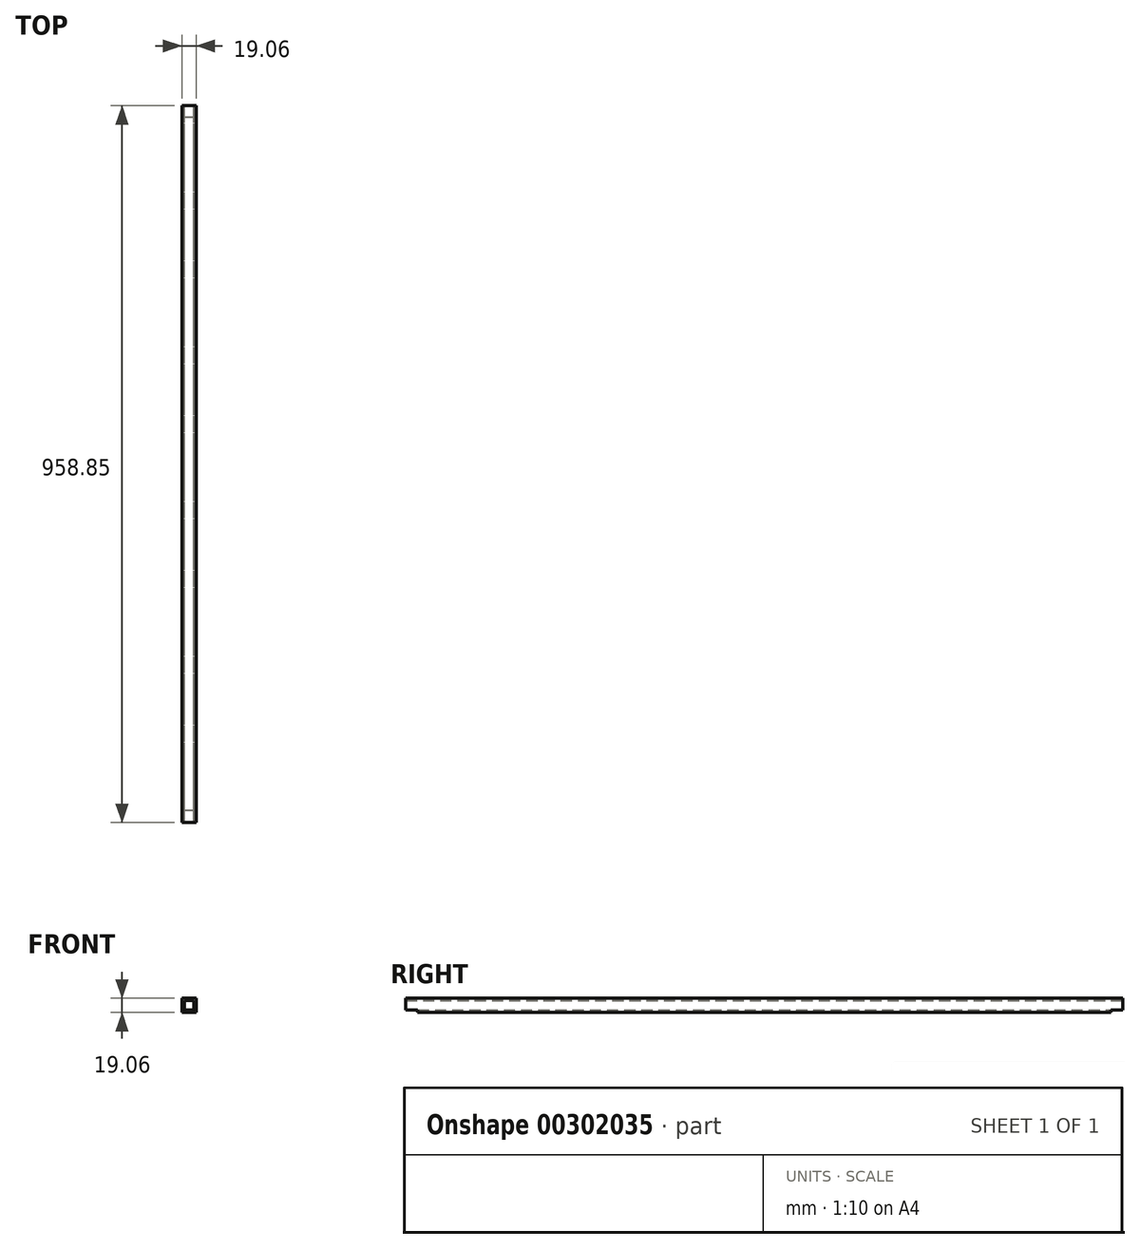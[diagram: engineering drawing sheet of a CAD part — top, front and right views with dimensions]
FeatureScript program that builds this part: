
annotation { "Feature Type Name" : "Feature", "Feature Type Description" : "" }
export const myFeature = defineFeature(function(context is Context, id is Id, definition is map)
    precondition{}
    {
        {
            var Q0;
            Q0=qCreatedBy(makeId("Front.planeOp"),FACE);
            var sketch = newSketch(context, id + "F0", { "sketchPlane" : qUnion([Q0])});
            skLineSegment(sketch, "E0.bottom", {"start": v(9.52, 9.53) * mm, "end": v(-9.53, 9.52) * mm});
            skLineSegment(sketch, "E0.top", {"start": v(9.53, -9.52) * mm, "end": v(-9.52, -9.53) * mm});
            skLineSegment(sketch, "E0.left", {"start": v(9.52, 9.53) * mm, "end": v(9.53, -9.52) * mm});
            skLineSegment(sketch, "E0.right", {"start": v(-9.53, 9.52) * mm, "end": v(-9.52, -9.53) * mm});
            skPoint(sketch, "E0.middle", {"position": v(0, 0) * mm});
            skLineSegment(sketch, "E1.bottom", {"start": v(6.35, 6.35) * mm, "end": v(-6.35, 6.35) * mm});
            skLineSegment(sketch, "E1.top", {"start": v(6.35, -6.35) * mm, "end": v(-6.35, -6.35) * mm});
            skLineSegment(sketch, "E1.left", {"start": v(6.35, 6.35) * mm, "end": v(6.35, -6.35) * mm});
            skLineSegment(sketch, "E1.right", {"start": v(-6.35, 6.35) * mm, "end": v(-6.35, -6.35) * mm});
            skSolve(sketch);
        }
        {
            var Q0;
            Q0=qSketchRegion(id+"F0",true);
            extrude(context, id + "F1", {"entities" : qUnion([Q0]), "depth" : 958.85 * mm});
        }
        {
            var Q0;
            Q0=makeQuery(id+"F1.opExtrude","SWEPT_FACE",FACE,{"disambiguationData":[OSD([sQuery(id+"F0.wireOp",EDGE,"E0.right")])]});
            var sketch = newSketch(context, id + "F2", { "sketchPlane" : qUnion([Q0])});
            skLineSegment(sketch, "E2.bottom", {"start": v(0, -9.53) * mm, "end": v(15.88, -9.53) * mm});
            skLineSegment(sketch, "E2.top", {"start": v(0, -6.35) * mm, "end": v(15.88, -6.35) * mm});
            skLineSegment(sketch, "E2.left", {"start": v(0, -9.53) * mm, "end": v(0, -6.35) * mm});
            skLineSegment(sketch, "E2.right", {"start": v(15.88, -9.53) * mm, "end": v(15.88, -6.35) * mm});
            skLineSegment(sketch, "E3.bottom", {"start": v(958.85, -9.53) * mm, "end": v(942.98, -9.53) * mm});
            skLineSegment(sketch, "E3.top", {"start": v(958.85, -6.35) * mm, "end": v(942.98, -6.35) * mm});
            skLineSegment(sketch, "E3.left", {"start": v(958.85, -9.53) * mm, "end": v(958.85, -6.35) * mm});
            skLineSegment(sketch, "E3.right", {"start": v(942.98, -9.53) * mm, "end": v(942.98, -6.35) * mm});
            skSolve(sketch);
        }
        {
            var Q0;
            Q0=qSketchRegion(id+"F2",true);
            extrude(context, id + "F3", {"entities" : qUnion([Q0]), "operationType" : NewBodyOperationType.REMOVE, "oppositeDirection" : true, "depth" : 19.05 * mm});
        }
    });
